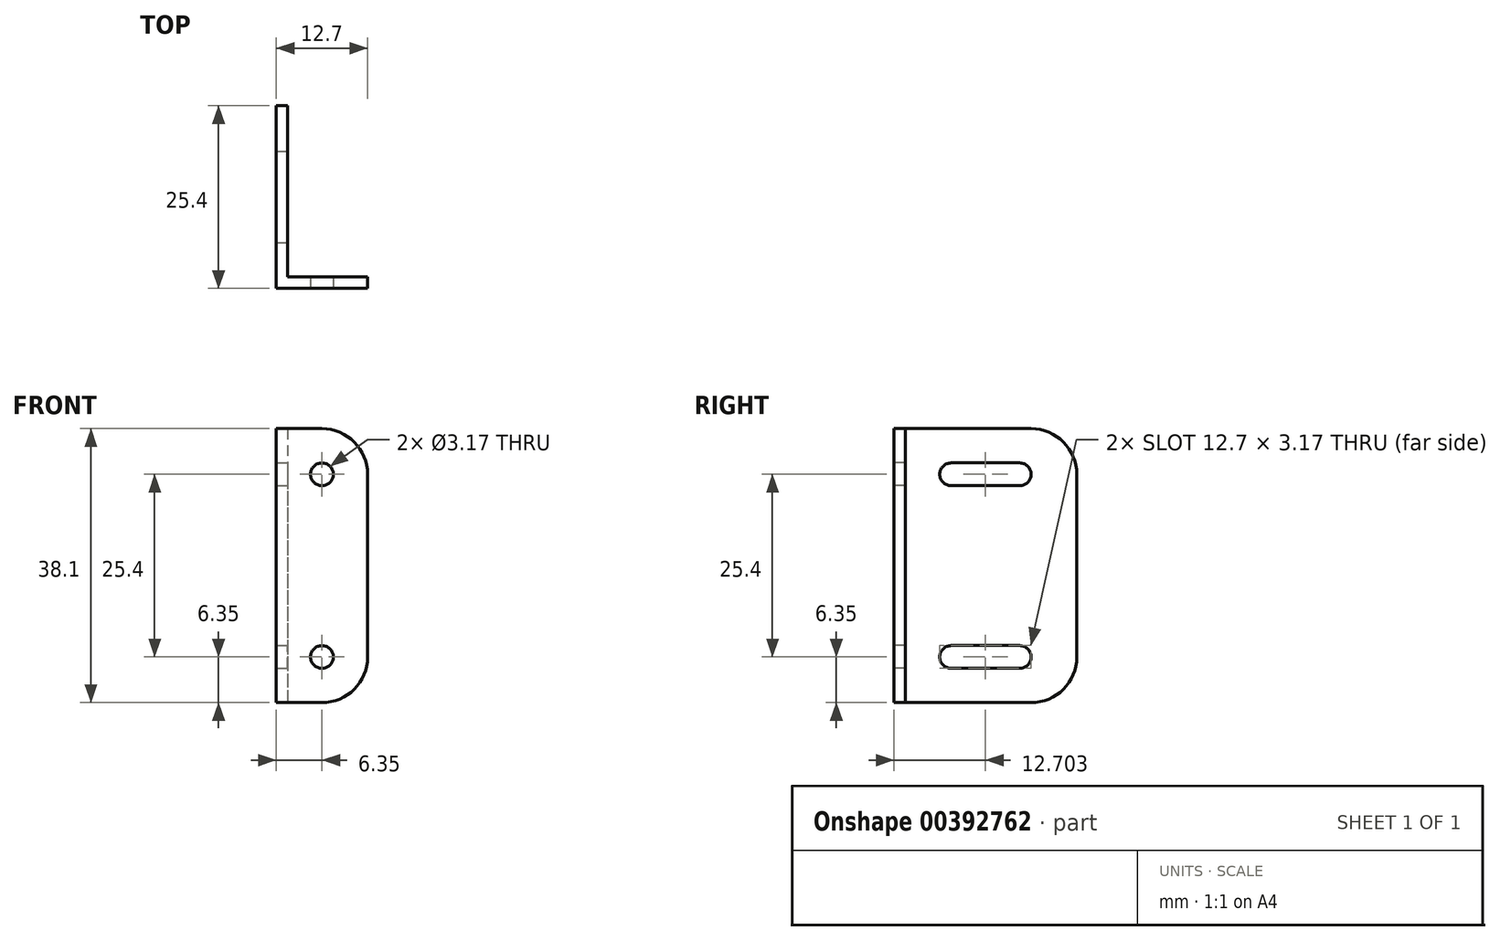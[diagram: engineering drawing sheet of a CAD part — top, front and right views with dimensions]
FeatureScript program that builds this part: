
annotation { "Feature Type Name" : "Feature", "Feature Type Description" : "" }
export const myFeature = defineFeature(function(context is Context, id is Id, definition is map)
    precondition{}
    {
        {
            var Q0;
            Q0=qCreatedBy(makeId("Front.planeOp"),FACE);
            var sketch = newSketch(context, id + "F0", { "sketchPlane" : qUnion([Q0])});
            skLineSegment(sketch, "E0.bottom", {"start": v(6.35, 19.05) * mm, "end": v(-6.35, 19.05) * mm});
            skLineSegment(sketch, "E0.top", {"start": v(6.35, -19.05) * mm, "end": v(-6.35, -19.05) * mm});
            skLineSegment(sketch, "E0.left", {"start": v(6.35, 19.05) * mm, "end": v(6.35, -19.05) * mm});
            skLineSegment(sketch, "E0.right", {"start": v(-6.35, 19.05) * mm, "end": v(-6.35, -19.05) * mm});
            skPoint(sketch, "E0.middle", {"position": v(0, 0) * mm});
            skSolve(sketch);
        }
        {
            var Q0;
            Q0 = qSketchRegion(id + "F0", true);
            extrude(context, id + "F1", {"entities" : qUnion([Q0]), "depth" : 1.59 * mm});
        }
        {
            var Q0;
            Q0=makeQuery(id+"F1.opExtrude","CAP_FACE",FACE,{"disambiguationData":[OSD([sQuery(id+"F0.wireOp",EDGE,"E0.bottom"),sQuery(id+"F0.wireOp",EDGE,"E0.top"),sQuery(id+"F0.wireOp",EDGE,"E0.left"),sQuery(id+"F0.wireOp",EDGE,"E0.right")])],"isStart":false});
            var sketch = newSketch(context, id + "F2", { "sketchPlane" : qUnion([Q0])});
            skLineSegment(sketch, "E1.bottom", {"start": v(-6.35, 19.05) * mm, "end": v(-4.76, 19.05) * mm});
            skLineSegment(sketch, "E1.top", {"start": v(-6.35, -19.05) * mm, "end": v(-4.76, -19.05) * mm});
            skLineSegment(sketch, "E1.left", {"start": v(-6.35, 19.05) * mm, "end": v(-6.35, -19.05) * mm});
            skLineSegment(sketch, "E1.right", {"start": v(-4.76, 19.05) * mm, "end": v(-4.76, -19.05) * mm});
            skSolve(sketch);
        }
        {
            var Q0;
            Q0 = qSketchRegion(id + "F2", true);
            extrude(context, id + "F3", {"entities" : qUnion([Q0]), "operationType" : NewBodyOperationType.ADD, "oppositeDirection" : true, "depth" : 25.4 * mm});
        }
        {
            var Q0;
            Q0=makeQuery(id+"F1.opExtrude","SWEPT_EDGE",EDGE,{"disambiguationData":[OSD([sQuery(id+"F0.wireOp",EDGE,"E0.bottom"),sQuery(id+"F0.wireOp",EDGE,"E0.left")])]});
            var Q1;
            Q1=makeQuery(id+"F3.opExtrude","CAP_EDGE",EDGE,{"disambiguationData":[OSD([sQuery(id+"F2.wireOp",EDGE,"E1.bottom")])],"isStart":false});
            var Q2;
            Q2=makeQuery(id+"F1.opExtrude","SWEPT_EDGE",EDGE,{"disambiguationData":[OSD([sQuery(id+"F0.wireOp",EDGE,"E0.top"),sQuery(id+"F0.wireOp",EDGE,"E0.left")])]});
            var Q3;
            Q3=makeQuery(id+"F3.opExtrude","CAP_EDGE",EDGE,{"disambiguationData":[OSD([sQuery(id+"F2.wireOp",EDGE,"E1.top")])],"isStart":false});
            fillet(context, id + "F4", {"entities" : qUnion([Q0, Q1, Q2, Q3]), "radius" : 6.35 * mm, "tangentPropagation" : true, "allowEdgeOverflow" : false});
        }
        {
            var Q0;
            Q0=makeQuery(id+"F1.opExtrude","CAP_FACE",FACE,{"disambiguationData":[OSD([sQuery(id+"F0.wireOp",EDGE,"E0.bottom"),sQuery(id+"F0.wireOp",EDGE,"E0.top"),sQuery(id+"F0.wireOp",EDGE,"E0.left"),sQuery(id+"F0.wireOp",EDGE,"E0.right")])],"isStart":false});
            var sketch = newSketch(context, id + "F5", { "sketchPlane" : qUnion([Q0])});
            skCircle(sketch, "E2", {"center": v(0, 12.7) * mm, "radius": 1.59 * mm});
            skCircle(sketch, "E3", {"center": v(0, -12.7) * mm, "radius": 1.59 * mm});
            skLineSegment(sketch, "E4", {"start": v(0, 12.7) * mm, "end": v(0, 0) * mm, "construction": true});
            skLineSegment(sketch, "E5", {"start": v(0, 0) * mm, "end": v(0, -12.7) * mm, "construction": true});
            skSolve(sketch);
        }
        {
            var Q0;
            Q0 = qSketchRegion(id + "F5", true);
            extrude(context, id + "F6", {"entities" : qUnion([Q0]), "operationType" : NewBodyOperationType.REMOVE, "endBound" : BoundingType.UP_TO_NEXT, "oppositeDirection" : true, "depth" : 25.4 * mm});
        }
        {
            var Q0;
            Q0=makeQuery(id+"F3.opExtrude","SWEPT_FACE",FACE,{"disambiguationData":[OSD([sQuery(id+"F2.wireOp",EDGE,"E1.right")])]});
            var sketch = newSketch(context, id + "F7", { "sketchPlane" : qUnion([Q0])});
            skLineSegment(sketch, "E6.bottom", {"start": v(6.35, 14.29) * mm, "end": v(15.88, 14.29) * mm});
            skLineSegment(sketch, "E6.top", {"start": v(6.35, 11.11) * mm, "end": v(15.88, 11.11) * mm});
            skLineSegment(sketch, "E6.left", {"start": v(6.35, 14.29) * mm, "end": v(6.35, 11.11) * mm});
            skLineSegment(sketch, "E6.right", {"start": v(15.88, 14.29) * mm, "end": v(15.87, 11.11) * mm});
            skLineSegment(sketch, "E7.bottom", {"start": v(6.35, -11.11) * mm, "end": v(15.88, -11.11) * mm});
            skLineSegment(sketch, "E7.top", {"start": v(6.35, -14.29) * mm, "end": v(15.88, -14.29) * mm});
            skLineSegment(sketch, "E7.left", {"start": v(6.35, -11.11) * mm, "end": v(6.35, -14.29) * mm});
            skLineSegment(sketch, "E7.right", {"start": v(15.88, -11.11) * mm, "end": v(15.88, -14.29) * mm});
            skLineSegment(sketch, "E8", {"start": v(11.11, 11.11) * mm, "end": v(11.11, -11.11) * mm, "construction": true});
            skLineSegment(sketch, "E9", {"start": v(0, 0) * mm, "end": v(11.11, 0) * mm, "construction": true});
            skLineSegment(sketch, "E10", {"start": v(6.35, 12.7) * mm, "end": v(15.88, 12.7) * mm, "construction": true});
            skLineSegment(sketch, "E11", {"start": v(6.35, -12.7) * mm, "end": v(15.88, -12.7) * mm, "construction": true});
            skCircle(sketch, "E12", {"center": v(6.35, 12.7) * mm, "radius": 1.59 * mm});
            skCircle(sketch, "E13", {"center": v(15.88, 12.7) * mm, "radius": 1.59 * mm});
            skCircle(sketch, "E14", {"center": v(6.35, -12.7) * mm, "radius": 1.59 * mm});
            skCircle(sketch, "E15", {"center": v(15.88, -12.7) * mm, "radius": 1.59 * mm});
            skSolve(sketch);
        }
        {
            var Q0;
            Q0 = qSketchRegion(id + "F7", true);
            extrude(context, id + "F8", {"entities" : qUnion([Q0]), "operationType" : NewBodyOperationType.REMOVE, "endBound" : BoundingType.UP_TO_NEXT, "oppositeDirection" : true, "depth" : 25.4 * mm});
        }
    });
